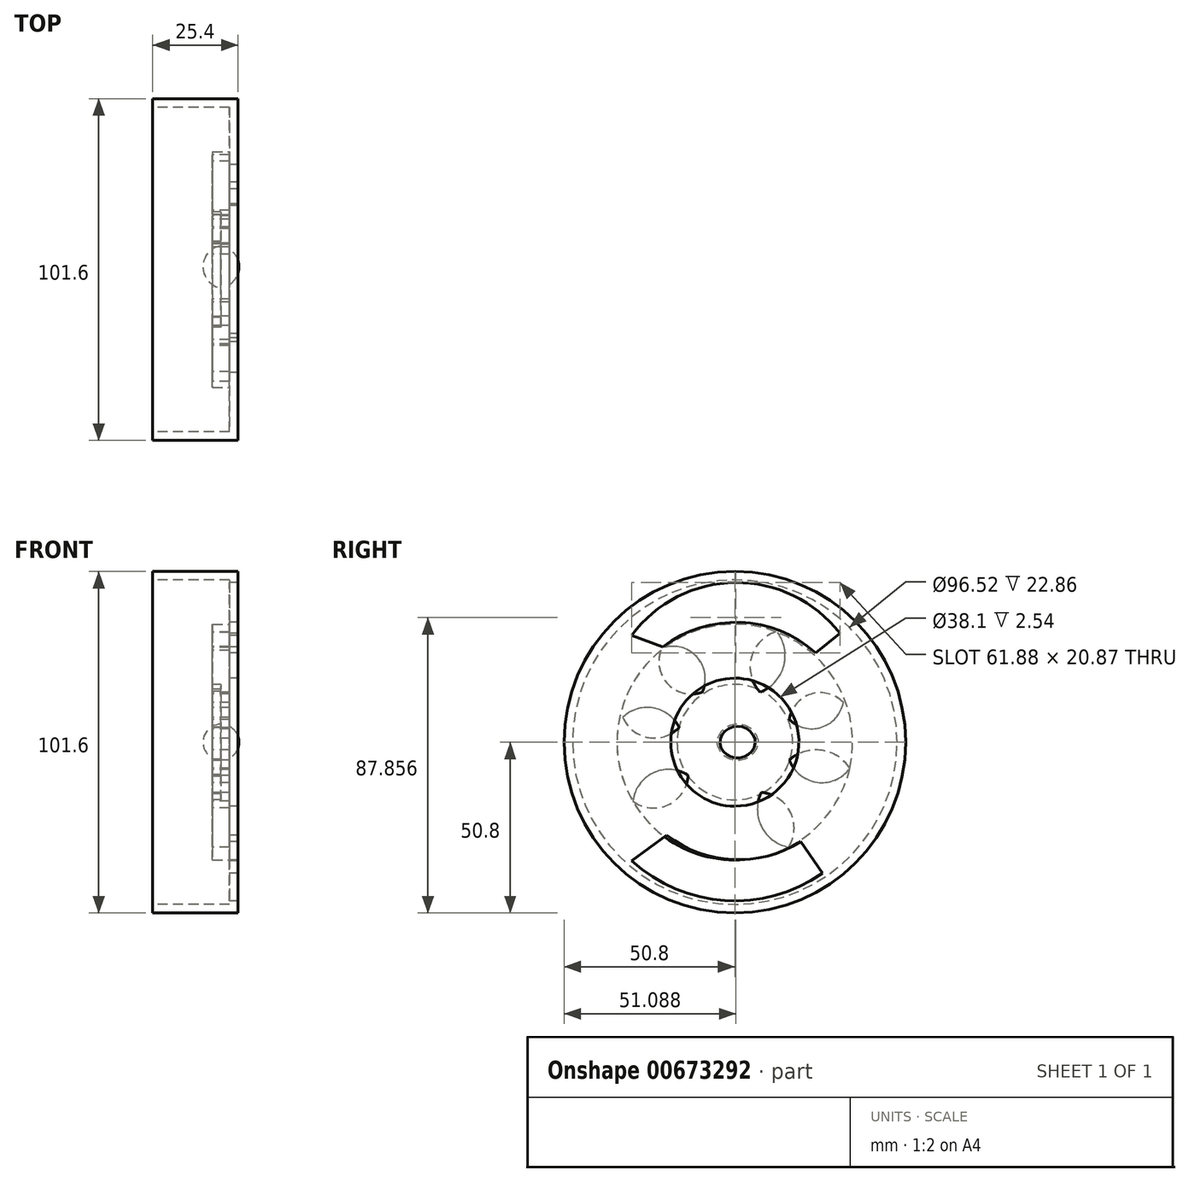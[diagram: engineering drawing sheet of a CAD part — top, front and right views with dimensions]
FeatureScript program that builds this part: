
annotation { "Feature Type Name" : "Feature", "Feature Type Description" : "" }
export const myFeature = defineFeature(function(context is Context, id is Id, definition is map)
    precondition{}
    {
        {
            var Q0;
            Q0=qCreatedBy(makeId("Right.planeOp"),FACE);
            var sketch = newSketch(context, id + "F0", { "sketchPlane" : qUnion([Q0])});
            skCircle(sketch, "E0", {"center": v(0, 0) * mm, "radius": 50.8 * mm});
            skSolve(sketch);
        }
        {
            var Q0;
            Q0=makeQuery(id+"F0.imprint","IMPRINT",FACE,{"disambiguationData":[TD([[makeQuery(id+"F0.imprint","IMPRINT",EDGE,{"derivedFrom":sQuery(id+"F0.wireOp",EDGE,"E0")}),1.0]])]});
            extrude(context, id + "F1", {"entities" : qUnion([Q0]), "depth" : 25.4 * mm, "offsetDistance" : 25.4 * mm});
        }
        {
            var Q0;
            Q0=makeQuery(id+"F1.opExtrude","CAP_FACE",FACE,{"disambiguationData":[OSD([sQuery(id+"F0.wireOp",EDGE,"E0")])],"isStart":true});
            var sketch = newSketch(context, id + "F2", { "sketchPlane" : qUnion([Q0])});
            skCircle(sketch, "E1", {"center": v(0, 0) * mm, "radius": 48.26 * mm});
            skSolve(sketch);
        }
        {
            var Q0;
            Q0=makeQuery(id+"F2.imprint","IMPRINT",FACE,{"disambiguationData":[TD([[makeQuery(id+"F2.imprint","IMPRINT",EDGE,{"derivedFrom":sQuery(id+"F2.wireOp",EDGE,"E1")}),1.0]])]});
            extrude(context, id + "F3", {"entities" : qUnion([Q0]), "operationType" : NewBodyOperationType.REMOVE, "oppositeDirection" : true, "depth" : 22.86 * mm, "offsetDistance" : 25.4 * mm});
        }
        {
            var Q0;
            Q0=makeQuery(id+"F3.boolean.opBoolean","COPY",FACE,{"derivedFrom":makeQuery(id+"F3.opExtrude","CAP_FACE",FACE,{"disambiguationData":[OSD([sQuery(id+"F2.wireOp",EDGE,"E1")])],"isStart":false})});
            var sketch = newSketch(context, id + "F4", { "sketchPlane" : qUnion([Q0])});
            skCircle(sketch, "E2", {"center": v(0, 0) * mm, "radius": 35.05 * mm});
            skSolve(sketch);
        }
        {
            var Q0;
            Q0=makeQuery(id+"F3.boolean.opBoolean","COPY",FACE,{"derivedFrom":makeQuery(id+"F3.opExtrude","CAP_FACE",FACE,{"disambiguationData":[OSD([sQuery(id+"F2.wireOp",EDGE,"E1")])],"isStart":false})});
            var sketch = newSketch(context, id + "F5", { "sketchPlane" : qUnion([Q0])});
            skArc(sketch, "E3", {"start": v(21.44, 28.35) * mm, "mid": v(-1.6, 35.65) * mm, "end": v(-24.03, 26.62) * mm});
            skLineSegment(sketch, "E4", {"start": v(-24.03, 26.62) * mm, "end": v(-31.23, 32.38) * mm});
            skLineSegment(sketch, "E5", {"start": v(21.44, 28.35) * mm, "end": v(30.65, 31.8) * mm});
            skArc(sketch, "E6", {"start": v(30.65, 31.8) * mm, "mid": v(-0.14, 47.49) * mm, "end": v(-31.23, 32.38) * mm});
            skSolve(sketch);
        }
        {
            var Q0;
            Q0 = qSketchRegion(id + "F5", true);
            extrude(context, id + "F6", {"entities" : qUnion([Q0]), "operationType" : NewBodyOperationType.REMOVE, "oppositeDirection" : true, "depth" : 25.4 * mm, "offsetDistance" : 25.4 * mm});
        }
        {
            var Q0;
            Q0=makeQuery(id+"F3.boolean.opBoolean","COPY",FACE,{"derivedFrom":makeQuery(id+"F3.opExtrude","CAP_FACE",FACE,{"disambiguationData":[OSD([sQuery(id+"F2.wireOp",EDGE,"E1")])],"isStart":false})});
            var sketch = newSketch(context, id + "F7", { "sketchPlane" : qUnion([Q0])});
            skLineSegment(sketch, "E7", {"start": v(66.35, 0) * mm, "end": v(-69.43, 0) * mm});
            skSolve(sketch);
        }
        {
            var Q0;
            {var subQ0=sQuery(id+"F7.wireOp",EDGE,"E7");var subQ1=makeQuery(id+"F3.boolean.opBoolean","COPY",EDGE,{"derivedFrom":makeQuery(id+"F3.opExtrude","CAP_EDGE",EDGE,{"disambiguationData":[OSD([sQuery(id+"F2.wireOp",EDGE,"E1")])],"isStart":false})});var subQ2=makeQuery(id+"F7.imprint","INTERSECT",VERTEX,{"disambiguationData":[OD(0.0)],"derivedFrom":[subQ1,subQ0]});Q0=makeQuery(id+"F7.imprint","IMPRINT",FACE,{"disambiguationData":[TD([[makeQuery(id+"F7.imprint","IMPRINT",EDGE,{"disambiguationData":[TD([[subQ2,-1.0]])],"derivedFrom":subQ0}),1.0]])]});}
            var sketch = newSketch(context, id + "F8", { "sketchPlane" : qUnion([Q0])});
            skArc(sketch, "E8", {"start": v(-19.58, -29.56) * mm, "mid": v(0.65, -34.94) * mm, "end": v(20.26, -27.63) * mm});
            skLineSegment(sketch, "E9", {"start": v(-19.58, -29.56) * mm, "end": v(-26.05, -39) * mm});
            skLineSegment(sketch, "E10", {"start": v(20.26, -27.63) * mm, "end": v(30.65, -35.26) * mm});
            skArc(sketch, "E11", {"start": v(-26.05, -39) * mm, "mid": v(2.96, -47.1) * mm, "end": v(30.65, -35.26) * mm});
            skSolve(sketch);
        }
        {
            var Q0;
            Q0=makeQuery(id+"F8.imprint","IMPRINT",FACE,{"disambiguationData":[TD([[makeQuery(id+"F8.imprint","IMPRINT",EDGE,{"derivedFrom":sQuery(id+"F8.wireOp",EDGE,"E8")}),-1.0]])]});
            extrude(context, id + "F9", {"entities" : qUnion([Q0]), "operationType" : NewBodyOperationType.REMOVE, "oppositeDirection" : true, "depth" : 25.4 * mm, "offsetDistance" : 25.4 * mm});
        }
        {
            var Q0;
            Q0=qCreatedBy(makeId("Right.planeOp"),FACE);
            var sketch = newSketch(context, id + "F10", { "sketchPlane" : qUnion([Q0])});
            skCircle(sketch, "E12", {"center": v(0, 0) * mm, "radius": 19.05 * mm});
            skSolve(sketch);
        }
        {
            var Q0;
            Q0 = qSketchRegion(id + "F10", true);
            extrude(context, id + "F11", {"entities" : qUnion([Q0]), "operationType" : NewBodyOperationType.REMOVE, "oppositeDirection" : true, "depth" : 2.54 * mm, "offsetDistance" : 25.4 * mm});
        }
        {
            var Q0;
            Q0 = qSketchRegion(id + "F10", true);
            extrude(context, id + "F12", {"entities" : qUnion([Q0]), "operationType" : NewBodyOperationType.REMOVE, "depth" : 25.4 * mm, "offsetDistance" : 25.4 * mm});
        }
        {
            var Q0;
            Q0=makeQuery(id+"F5.imprint","IMPRINT",FACE,{"disambiguationData":[TD([[makeQuery(id+"F5.imprint","IMPRINT",EDGE,{"derivedFrom":sQuery(id+"F5.wireOp",EDGE,"E3")}),1.0]])]});
            var sketch = newSketch(context, id + "F13", { "sketchPlane" : qUnion([Q0])});
            skCircle(sketch, "E13", {"center": v(0, 0) * mm, "radius": 19.06 * mm});
            skSolve(sketch);
        }
        {
            var Q0;
            Q0 = qSketchRegion(id + "F13", true);
            extrude(context, id + "F14", {"entities" : qUnion([Q0]), "operationType" : NewBodyOperationType.REMOVE, "depth" : 12.7 * mm, "offsetDistance" : 25.4 * mm});
        }
        {
            var Q0;
            Q0 = qSketchRegion(id + "F4", true);
            extrude(context, id + "F15", {"entities" : qUnion([Q0]), "operationType" : NewBodyOperationType.ADD, "depth" : 5.08 * mm, "offsetDistance" : 25.4 * mm});
        }
        {
            var Q0;
            Q0=makeQuery(id+"F15.opExtrude","CAP_FACE",FACE,{"disambiguationData":[OSD([sQuery(id+"F4.wireOp",EDGE,"E2")])],"isStart":false});
            var sketch = newSketch(context, id + "F16", { "sketchPlane" : qUnion([Q0])});
            skCircle(sketch, "E14", {"center": v(0, 0) * mm, "radius": 17.19 * mm});
            skSolve(sketch);
        }
        {
            var Q0;
            Q0 = qSketchRegion(id + "F16", true);
            extrude(context, id + "F17", {"entities" : qUnion([Q0]), "operationType" : NewBodyOperationType.REMOVE, "oppositeDirection" : true, "depth" : 2.54 * mm, "offsetDistance" : 25.4 * mm});
        }
        {
            var Q0;
            Q0 = qSketchRegion(id + "F16", true);
            extrude(context, id + "F18", {"entities" : qUnion([Q0]), "operationType" : NewBodyOperationType.REMOVE, "oppositeDirection" : true, "depth" : 2.54 * mm, "offsetDistance" : 25.4 * mm});
        }
        {
            var Q0;
            Q0=makeQuery(id+"F17.boolean.opBoolean","COPY",FACE,{"derivedFrom":makeQuery(id+"F17.opExtrude","CAP_FACE",FACE,{"disambiguationData":[OSD([sQuery(id+"F16.wireOp",EDGE,"E14")])],"isStart":false})});
            var sketch = newSketch(context, id + "F19", { "sketchPlane" : qUnion([Q0])});
            skArc(sketch, "E15", {"start": v(-7.09, 0) * mm, "mid": v(-0.82, -5.36) * mm, "end": v(5.46, 0) * mm});
            skLineSegment(sketch, "E16", {"start": v(56.53, 0) * mm, "end": v(-60.05, 0) * mm});
            skSolve(sketch);
        }
        {
            var Q0;
            {var subQ0=sQuery(id+"F19.wireOp",EDGE,"E15");Q0=makeQuery(id+"F19.imprint","IMPRINT",FACE,{"disambiguationData":[TD([[makeQuery(id+"F19.imprint","IMPRINT",EDGE,{"derivedFrom":subQ0}),1.0]])]});}
            var Q1;
            Q1=sQuery(id+"F19.wireOp",EDGE,"E16");
            revolve(context, id + "F20", {"operationType" : NewBodyOperationType.ADD, "entities" : qUnion([Q0]), "axis" : qUnion([Q1]), "revolveType" : RevolveType.FULL});
        }
        {
            var Q0;
            Q0=makeQuery(id+"F15.opExtrude","CAP_FACE",FACE,{"disambiguationData":[OSD([sQuery(id+"F4.wireOp",EDGE,"E2")])],"isStart":false});
            var sketch = newSketch(context, id + "F21", { "sketchPlane" : qUnion([Q0])});
            skArc(sketch, "E17", {"start": v(0, -35.05) * mm, "mid": v(7.62, -26.12) * mm, "end": v(0, -17.19) * mm});
            skLineSegment(sketch, "E18", {"start": v(7.62, -26.12) * mm, "end": v(0, -26.12) * mm});
            skArc(sketch, "E19", {"start": v(0, -17.19) * mm, "mid": v(-7.62, -26.12) * mm, "end": v(0, -35.05) * mm});
            skLineSegment(sketch, "E20", {"start": v(0, -26.12) * mm, "end": v(-7.62, -26.12) * mm});
            skSolve(sketch);
        }
        {
            var Q0;
            {var subQ2=makeQuery(id+"F15.opExtrude","CAP_EDGE",EDGE,{"disambiguationData":[OSD([sQuery(id+"F4.wireOp",EDGE,"E2")])],"isStart":false});Q0=makeQuery(id+"F21.imprint","IMPRINT",FACE,{"disambiguationData":[TD([[makeQuery(id+"F21.imprint","IMPRINT",EDGE,{"derivedFrom":subQ2}),1.0]])]});}
            var sketch = newSketch(context, id + "F22", { "sketchPlane" : qUnion([Q0])});
            skArc(sketch, "E21", {"start": v(-29.42, -16.86) * mm, "mid": v(-19.31, -19.58) * mm, "end": v(-14.56, -10.25) * mm});
            skArc(sketch, "E22", {"start": v(-14.56, -10.25) * mm, "mid": v(-25.54, -5.59) * mm, "end": v(-29.42, -16.86) * mm});
            skLineSegment(sketch, "E23", {"start": v(-17.86, -18.75) * mm, "end": v(-25.54, -5.59) * mm});
            skSolve(sketch);
        }
        {
            var Q0;
            {var subQ9=makeQuery(id+"F15.opExtrude","CAP_EDGE",EDGE,{"disambiguationData":[OSD([sQuery(id+"F4.wireOp",EDGE,"E2")])],"isStart":false});Q0=makeQuery(id+"F22.imprint","IMPRINT",FACE,{"disambiguationData":[TD([[makeQuery(id+"F22.imprint","IMPRINT",EDGE,{"derivedFrom":makeQuery(id+"F21.imprint","IMPRINT",EDGE,{"derivedFrom":subQ9})}),1.0]])]});}
            var sketch = newSketch(context, id + "F23", { "sketchPlane" : qUnion([Q0])});
            skPoint(sketch, "E24.endSnap0", {"position": v(-11.61, 19.85) * mm});
            skArc(sketch, "E25", {"start": v(-7.53, 14.88) * mm, "mid": v(-4.94, 25.3) * mm, "end": v(-12.52, 32.91) * mm});
            skArc(sketch, "E26", {"start": v(-12.52, 32.91) * mm, "mid": v(-14.55, 22.64) * mm, "end": v(-7.53, 14.88) * mm});
            skArc(sketch, "E27", {"start": v(21.78, 27.89) * mm, "mid": v(11.37, 25.45) * mm, "end": v(9.69, 14.88) * mm});
            skArc(sketch, "E28", {"start": v(9.69, 14.88) * mm, "mid": v(20, 17.41) * mm, "end": v(21.78, 27.89) * mm});
            skArc(sketch, "E29", {"start": v(33.32, 7.4) * mm, "mid": v(24.17, 10.17) * mm, "end": v(16.57, 4.37) * mm});
            skArc(sketch, "E30", {"start": v(16.57, 4.37) * mm, "mid": v(25.76, 1.39) * mm, "end": v(33.32, 7.4) * mm});
            skArc(sketch, "E31", {"start": v(30.31, -17.53) * mm, "mid": v(24.23, -9.14) * mm, "end": v(13.89, -9.84) * mm});
            skArc(sketch, "E32", {"start": v(13.89, -9.84) * mm, "mid": v(19.8, -18.61) * mm, "end": v(30.31, -17.53) * mm});
            skArc(sketch, "E33", {"start": v(-16.01, -31.2) * mm, "mid": v(-7.92, -25.09) * mm, "end": v(-7.87, -14.94) * mm});
            skArc(sketch, "E34", {"start": v(-7.87, -14.94) * mm, "mid": v(-16.51, -20.79) * mm, "end": v(-16.01, -31.2) * mm});
            skArc(sketch, "E35", {"start": v(-16.21, 6.78) * mm, "mid": v(-22.68, 14.3) * mm, "end": v(-32.26, 11.78) * mm});
            skArc(sketch, "E36", {"start": v(-32.26, 11.78) * mm, "mid": v(-25.74, 4.44) * mm, "end": v(-16.21, 6.78) * mm});
            skArc(sketch, "E37", {"start": v(-16.21, -5.26) * mm, "mid": v(-25.8, -2.42) * mm, "end": v(-34.2, -7.82) * mm});
            skArc(sketch, "E38", {"start": v(-34.2, -7.82) * mm, "mid": v(-24.44, -11.92) * mm, "end": v(-16.21, -5.26) * mm});
            skSolve(sketch);
        }
        {
            var Q0;
            Q0 = qSketchRegion(id + "F23", true);
            extrude(context, id + "F24", {"entities" : qUnion([Q0]), "operationType" : NewBodyOperationType.REMOVE, "oppositeDirection" : true, "depth" : 5.08 * mm, "offsetDistance" : 25.4 * mm});
        }
        {
            var Q0;
            Q0 = qSketchRegion(id + "F23", true);
            extrude(context, id + "F25", {"entities" : qUnion([Q0]), "operationType" : NewBodyOperationType.REMOVE, "oppositeDirection" : true, "depth" : 5.08 * mm, "offsetDistance" : 25.4 * mm});
        }
    });
